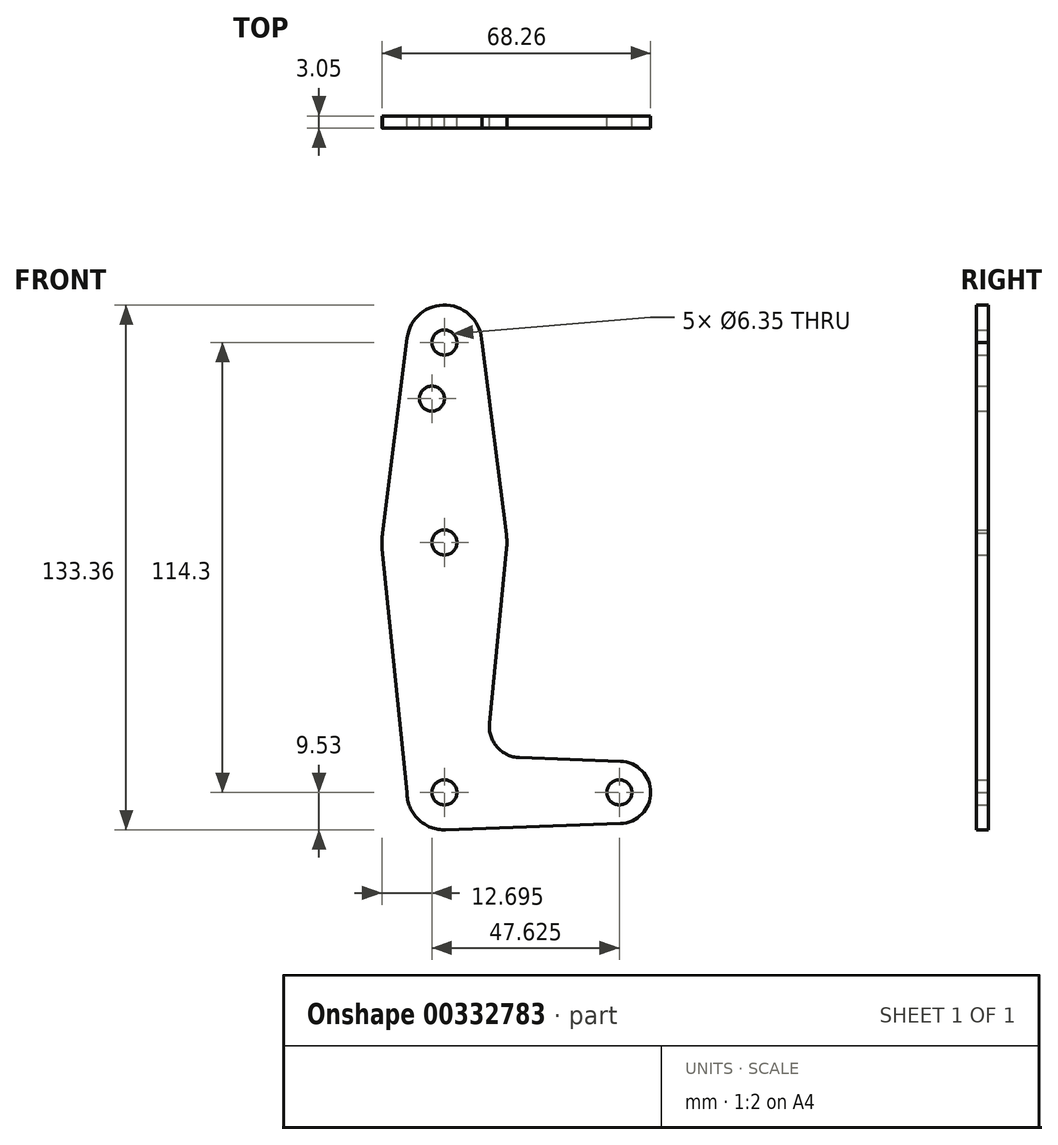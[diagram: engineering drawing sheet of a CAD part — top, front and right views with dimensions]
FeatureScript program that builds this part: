
annotation { "Feature Type Name" : "Feature", "Feature Type Description" : "" }
export const myFeature = defineFeature(function(context is Context, id is Id, definition is map)
    precondition{}
    {
        {
            var Q0;
            Q0=qCreatedBy(makeId("Front.planeOp"),FACE);
            var sketch = newSketch(context, id + "F0", { "sketchPlane" : qUnion([Q0])});
            skLineSegment(sketch, "E0", {"start": v(0, 114.3) * mm, "end": v(0, 0) * mm, "construction": true});
            skLineSegment(sketch, "E1", {"start": v(0, 0) * mm, "end": v(44.45, 0) * mm, "construction": true});
            skCircle(sketch, "E2", {"center": v(0, 0) * mm, "radius": 9.53 * mm});
            skCircle(sketch, "E3", {"center": v(0, 63.5) * mm, "radius": 15.88 * mm});
            skCircle(sketch, "E4", {"center": v(0, 114.3) * mm, "radius": 9.52 * mm});
            skCircle(sketch, "E5", {"center": v(44.45, 0) * mm, "radius": 7.94 * mm});
            skLineSegment(sketch, "E6", {"start": v(19.09, 8.85) * mm, "end": v(44.73, 7.93) * mm});
            skLineSegment(sketch, "E7", {"start": v(44.73, -7.93) * mm, "end": v(0, -9.53) * mm});
            skLineSegment(sketch, "E8", {"start": v(-9.53, 0) * mm, "end": v(-15.8, 61.9) * mm});
            skLineSegment(sketch, "E9", {"start": v(-15.8, 61.9) * mm, "end": v(-15.8, 65.1) * mm});
            skLineSegment(sketch, "E10", {"start": v(-15.8, 65.1) * mm, "end": v(-9.45, 115.49) * mm});
            skLineSegment(sketch, "E11", {"start": v(9.52, 114.3) * mm, "end": v(15.8, 65.1) * mm});
            skLineSegment(sketch, "E12", {"start": v(15.8, 61.95) * mm, "end": v(11.46, 17.57) * mm});
            skCircle(sketch, "E13", {"center": v(0, 114.3) * mm, "radius": 3.18 * mm});
            skCircle(sketch, "E14", {"center": v(0, 63.5) * mm, "radius": 3.18 * mm});
            skCircle(sketch, "E15", {"center": v(0, 0) * mm, "radius": 3.18 * mm});
            skCircle(sketch, "E16", {"center": v(44.45, 0) * mm, "radius": 3.18 * mm});
            skArc(sketch, "E17.filletArc", {"start": v(11.46, 17.57) * mm, "mid": v(13.39, 11.56) * mm, "end": v(19.09, 8.85) * mm});
            skCircle(sketch, "E18", {"center": v(-3.17, 100.03) * mm, "radius": 3.18 * mm});
            skSolve(sketch);
        }
        {
            var Q0;
            Q0 = qSketchRegion(id + "F0", true);
            extrude(context, id + "F1", {"entities" : qUnion([Q0]), "depth" : 3.05 * mm});
        }
    });
